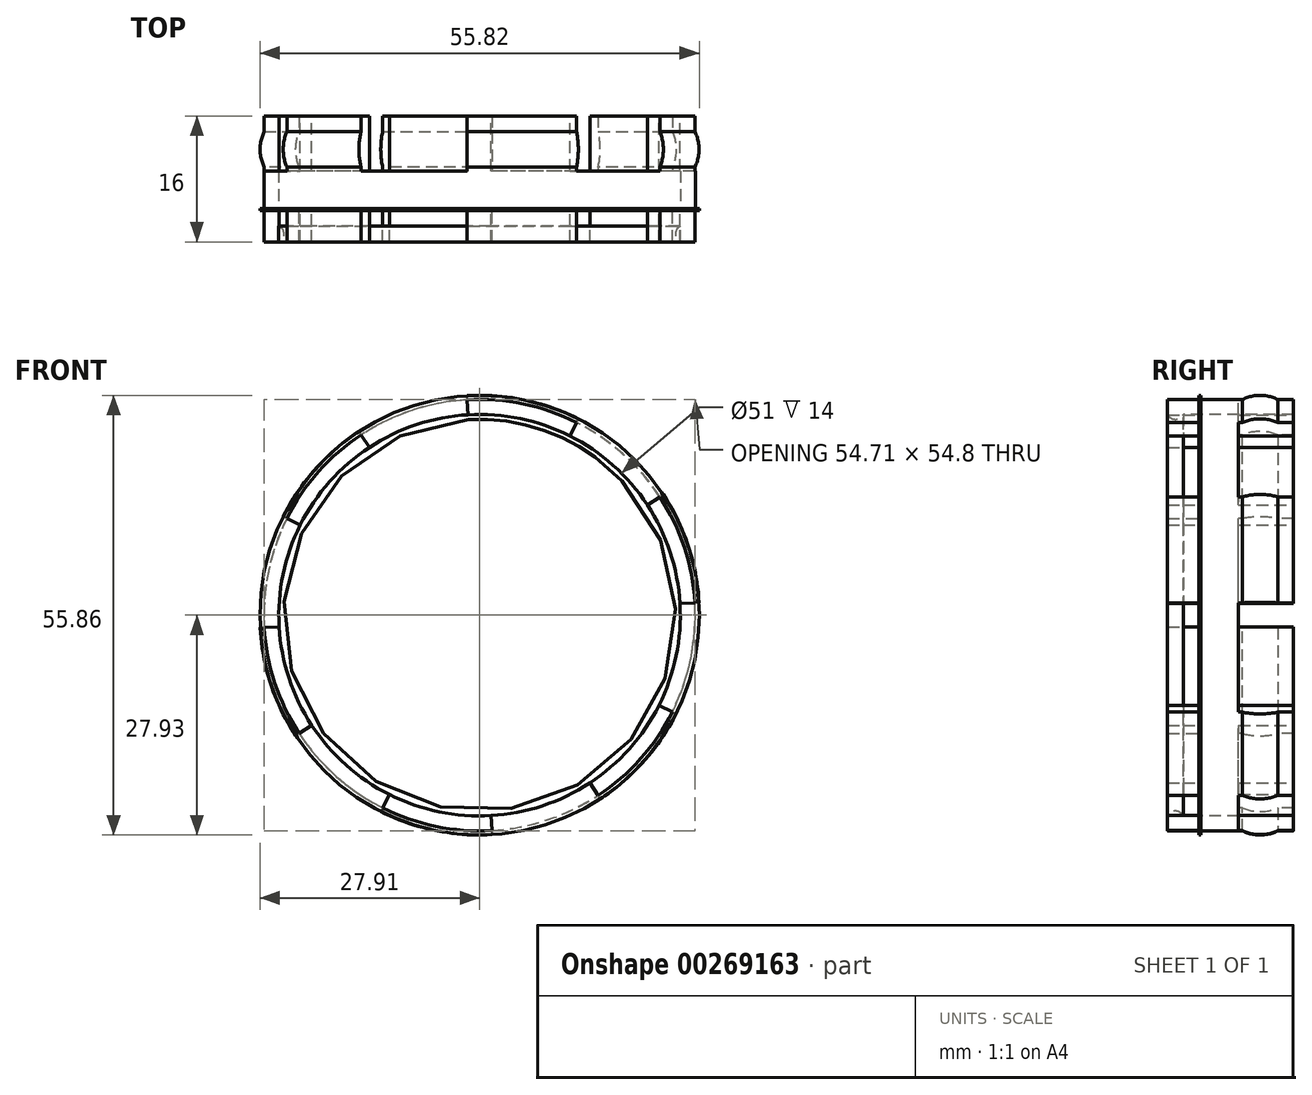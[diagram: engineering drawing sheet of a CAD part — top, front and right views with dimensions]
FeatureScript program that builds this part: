
annotation { "Feature Type Name" : "Feature", "Feature Type Description" : "" }
export const myFeature = defineFeature(function(context is Context, id is Id, definition is map)
    precondition{}
    {
        {
            var Q0;
            Q0=qCreatedBy(makeId("Front.planeOp"),FACE);
            var sketch = newSketch(context, id + "F0", { "sketchPlane" : qUnion([Q0])});
            skCircle(sketch, "E0", {"center": v(0, 0) * mm, "radius": 32.7 * mm});
            skCircle(sketch, "E1", {"center": v(0, 0) * mm, "radius": 27.2 * mm});
            skCircle(sketch, "E2", {"center": v(0, 0) * mm, "radius": 25.8 * mm});
            skSolve(sketch);
        }
        {
            var Q0;
            Q0=makeQuery(id+"F0.imprint","IMPRINT",FACE,{"disambiguationData":[TD([[makeQuery(id+"F0.imprint","IMPRINT",EDGE,{"derivedFrom":sQuery(id+"F0.wireOp",EDGE,"E0")}),1.0]])]});
            var Q1;
            Q1=makeQuery(id+"F0.imprint","IMPRINT",FACE,{"disambiguationData":[TD([[makeQuery(id+"F0.imprint","IMPRINT",EDGE,{"derivedFrom":sQuery(id+"F0.wireOp",EDGE,"E2")}),1.0]])]});
            var Q2;
            Q2=makeQuery(id+"F0.imprint","IMPRINT",FACE,{"disambiguationData":[TD([[makeQuery(id+"F0.imprint","IMPRINT",EDGE,{"derivedFrom":sQuery(id+"F0.wireOp",EDGE,"E1")}),1.0]])]});
            extrude(context, id + "F1", {"entities" : qUnion([Q0, Q1, Q2]), "depth" : 2 * mm});
        }
        {
            var Q0;
            Q0=makeQuery(id+"F1.opExtrude","CAP_FACE",FACE,{"disambiguationData":[OSD([sQuery(id+"F0.wireOp",EDGE,"E0")])],"isStart":true});
            var sketch = newSketch(context, id + "F2", { "sketchPlane" : qUnion([Q0])});
            skCircle(sketch, "E3", {"center": v(0, 0) * mm, "radius": 27.4 * mm});
            skCircle(sketch, "E4", {"center": v(0, 0) * mm, "radius": 25.5 * mm});
            skSolve(sketch);
        }
        {
            var Q0;
            Q0 = qSketchRegion(id + "F2", true);
            extrude(context, id + "F3", {"entities" : qUnion([Q0]), "operationType" : NewBodyOperationType.ADD, "depth" : 12 * mm});
        }
        {
            var Q0;
            {var subQ0=sQuery(id+"F0.wireOp",EDGE,"E0");Q0=makeQuery(id+"F3.boolean.opBoolean","SPLIT",FACE,{"disambiguationData":[TD([makeQuery(id+"F1.opExtrude","SWEPT_FACE",FACE,{"disambiguationData":[OSD([subQ0])]})])],"derivedFrom":makeQuery(id+"F1.opExtrude","CAP_FACE",FACE,{"disambiguationData":[OSD([subQ0])],"isStart":true})});}
            cPlane(context, id + "F4", {"entities" : qUnion([Q0]), "cplaneType" : CPlaneType.OFFSET, "offset" : 7.75 * mm, "width" : 152.4 * mm, "height" : 152.4 * mm});
        }
        {
            var Q0;
            Q0=qCreatedBy(makeId("Top.planeOp"),FACE);
            var sketch = newSketch(context, id + "F5", { "sketchPlane" : qUnion([Q0])});
            skLineSegment(sketch, "E5", {"start": v(27.4, 12) * mm, "end": v(27.4, 0) * mm});
            skArc(sketch, "E6", {"start": v(27.4, 5.5) * mm, "mid": v(27.93, 7.75) * mm, "end": v(27.4, 10) * mm});
            skSolve(sketch);
        }
        {
            var Q0;
            Q0=qCreatedBy(makeId("Right.planeOp"),FACE);
            var sketch = newSketch(context, id + "F6", { "sketchPlane" : qUnion([Q0])});
            skLineSegment(sketch, "E7", {"start": v(44.22, 0) * mm, "end": v(-14.52, 0) * mm});
            skSolve(sketch);
        }
        {
            var Q0;
            Q0 = qSketchRegion(id + "F5", true);
            var Q1;
            Q1=sQuery(id+"F6.wireOp",EDGE,"E7");
            revolve(context, id + "F7", {"operationType" : NewBodyOperationType.ADD, "entities" : qUnion([Q0]), "axis" : qUnion([Q1]), "revolveType" : RevolveType.FULL});
        }
        {
            var Q0;
            Q0=makeQuery(id+"F3.opExtrude","CAP_FACE",FACE,{"disambiguationData":[OSD([sQuery(id+"F2.wireOp",EDGE,"E3"),sQuery(id+"F2.wireOp",EDGE,"E4")])],"isStart":false});
            var sketch = newSketch(context, id + "F8", { "sketchPlane" : qUnion([Q0])});
            skArc(sketch, "E8.cCircle", {"start": v(-23.64, -11.9) * mm, "mid": v(-19.76, -17.6) * mm, "end": v(-14.53, -22.12) * mm, "construction": true});
            skLineSegment(sketch, "E8.1", {"start": v(15.04, 22.9) * mm, "end": v(24.48, 12.31) * mm});
            skLineSegment(sketch, "E8.3", {"start": v(27.35, -1.58) * mm, "end": v(22.9, -15.04) * mm});
            skLineSegment(sketch, "E8.5", {"start": v(12.31, -24.48) * mm, "end": v(-1.58, -27.35) * mm});
            skLineSegment(sketch, "E8.7", {"start": v(-15.04, -22.9) * mm, "end": v(-24.48, -12.31) * mm});
            skLineSegment(sketch, "E8.9", {"start": v(-27.35, 1.58) * mm, "end": v(-22.9, 15.04) * mm});
            skLineSegment(sketch, "E8.11", {"start": v(-12.31, 24.48) * mm, "end": v(1.58, 27.35) * mm});
            skPoint(sketch, "E8.0.midPoint", {"position": v(8.3, 25.13) * mm});
            skLineSegment(sketch, "E9", {"start": v(-27.35, 1.58) * mm, "end": v(0, 0) * mm});
            skLineSegment(sketch, "E10", {"start": v(-24.48, -12.31) * mm, "end": v(0, 0) * mm});
            skLineSegment(sketch, "E11", {"start": v(-24.48, -12.31) * mm, "end": v(-32.97, -16.58) * mm});
            skLineSegment(sketch, "E12", {"start": v(-27.35, 1.58) * mm, "end": v(-35.6, 2.05) * mm});
            skLineSegment(sketch, "E13", {"start": v(-35.6, 2.05) * mm, "end": v(-32.97, -16.58) * mm});
            skLineSegment(sketch, "E14", {"start": v(0, 0) * mm, "end": v(-15.04, -22.9) * mm});
            skLineSegment(sketch, "E15", {"start": v(-1.58, -27.35) * mm, "end": v(0, 0) * mm});
            skLineSegment(sketch, "E16", {"start": v(-15.04, -22.9) * mm, "end": v(-20.27, -30.87) * mm});
            skLineSegment(sketch, "E17", {"start": v(-1.58, -27.35) * mm, "end": v(-2.08, -36.1) * mm});
            skLineSegment(sketch, "E18", {"start": v(-2.08, -36.1) * mm, "end": v(-20.27, -30.87) * mm});
            skArc(sketch, "E19.trimOffspring", {"start": v(-1.52, -26.42) * mm, "mid": v(5.37, -25.92) * mm, "end": v(11.9, -23.64) * mm, "construction": true});
            skLineSegment(sketch, "E20", {"start": v(0, 0) * mm, "end": v(12.31, -24.48) * mm});
            skLineSegment(sketch, "E21", {"start": v(0, 0) * mm, "end": v(22.9, -15.04) * mm});
            skLineSegment(sketch, "E22", {"start": v(12.31, -24.48) * mm, "end": v(16.41, -32.63) * mm});
            skLineSegment(sketch, "E23", {"start": v(22.9, -15.04) * mm, "end": v(29.2, -19.18) * mm});
            skLineSegment(sketch, "E24", {"start": v(29.2, -19.18) * mm, "end": v(16.41, -32.63) * mm});
            skArc(sketch, "E25.trimOffspring", {"start": v(22.12, -14.53) * mm, "mid": v(25.13, -8.3) * mm, "end": v(26.42, -1.52) * mm, "construction": true});
            skLineSegment(sketch, "E26", {"start": v(0, 0) * mm, "end": v(24.48, 12.31) * mm});
            skLineSegment(sketch, "E27", {"start": v(27.35, -1.58) * mm, "end": v(0, 0) * mm});
            skLineSegment(sketch, "E28", {"start": v(27.35, -1.58) * mm, "end": v(35.67, -2.05) * mm});
            skLineSegment(sketch, "E29", {"start": v(24.48, 12.31) * mm, "end": v(31.5, 15.85) * mm});
            skLineSegment(sketch, "E30", {"start": v(31.5, 15.85) * mm, "end": v(35.67, -2.05) * mm});
            skArc(sketch, "E31.trimOffspring", {"start": v(23.64, 11.9) * mm, "mid": v(19.76, 17.6) * mm, "end": v(14.53, 22.12) * mm, "construction": true});
            skLineSegment(sketch, "E32", {"start": v(15.04, 22.9) * mm, "end": v(0, 0) * mm});
            skLineSegment(sketch, "E33", {"start": v(0, 0.13) * mm, "end": v(1.58, 27.35) * mm});
            skLineSegment(sketch, "E34", {"start": v(1.58, 27.35) * mm, "end": v(2.08, 36.13) * mm});
            skLineSegment(sketch, "E35", {"start": v(15.04, 22.9) * mm, "end": v(20.6, 31.37) * mm});
            skLineSegment(sketch, "E36", {"start": v(20.6, 31.37) * mm, "end": v(2.08, 36.13) * mm});
            skArc(sketch, "E37.trimOffspring", {"start": v(1.52, 26.42) * mm, "mid": v(-5.37, 25.92) * mm, "end": v(-11.9, 23.64) * mm, "construction": true});
            skLineSegment(sketch, "E38", {"start": v(0, 0) * mm, "end": v(-22.9, 15.04) * mm});
            skLineSegment(sketch, "E39", {"start": v(0, 0) * mm, "end": v(-12.31, 24.48) * mm});
            skLineSegment(sketch, "E40", {"start": v(-12.31, 24.48) * mm, "end": v(-16.96, 33.71) * mm});
            skLineSegment(sketch, "E41", {"start": v(-22.9, 15.04) * mm, "end": v(-31.87, 20.93) * mm});
            skLineSegment(sketch, "E42", {"start": v(-31.87, 20.93) * mm, "end": v(-16.96, 33.71) * mm});
            skArc(sketch, "E43.trimOffspring", {"start": v(-22.12, 14.53) * mm, "mid": v(-25.13, 8.3) * mm, "end": v(-26.42, 1.52) * mm, "construction": true});
            skCircle(sketch, "E44.0", {"center": v(0, 0) * mm, "radius": 32.7 * mm});
            skSolve(sketch);
        }
        {
            var Q0;
            {var subQ0=sQuery(id+"F8.wireOp",EDGE,"E9");var subQ3=makeQuery(id+"F3.opExtrude","CAP_EDGE",EDGE,{"disambiguationData":[OSD([sQuery(id+"F2.wireOp",EDGE,"E4")])],"isStart":false});var subQ4=makeQuery(id+"F8.imprint","INTERSECT",VERTEX,{"derivedFrom":[subQ3,subQ0]});Q0=makeQuery(id+"F8.imprint","IMPRINT",FACE,{"disambiguationData":[TD([[makeQuery(id+"F8.imprint","IMPRINT",EDGE,{"disambiguationData":[TD([[subQ4,-1.0]])],"derivedFrom":subQ3}),-1.0]])]});}
            var Q1;
            {var subQ0=sQuery(id+"F8.wireOp",EDGE,"E11");Q1=makeQuery(id+"F8.imprint","IMPRINT",FACE,{"disambiguationData":[TD([[makeQuery(id+"F8.imprint","IMPRINT",EDGE,{"derivedFrom":subQ0}),-1.0]])]});}
            var Q2;
            {var subQ0=sQuery(id+"F8.wireOp",EDGE,"E14");var subQ3=makeQuery(id+"F3.opExtrude","CAP_EDGE",EDGE,{"disambiguationData":[OSD([sQuery(id+"F2.wireOp",EDGE,"E4")])],"isStart":false});var subQ4=makeQuery(id+"F8.imprint","INTERSECT",VERTEX,{"derivedFrom":[subQ3,subQ0]});Q2=makeQuery(id+"F8.imprint","IMPRINT",FACE,{"disambiguationData":[TD([[makeQuery(id+"F8.imprint","IMPRINT",EDGE,{"disambiguationData":[TD([[subQ4,-1.0]])],"derivedFrom":subQ3}),-1.0]])]});}
            var Q3;
            {var subQ0=sQuery(id+"F8.wireOp",EDGE,"E16");Q3=makeQuery(id+"F8.imprint","IMPRINT",FACE,{"disambiguationData":[TD([[makeQuery(id+"F8.imprint","IMPRINT",EDGE,{"derivedFrom":subQ0}),1.0]])]});}
            var Q4;
            {var subQ0=sQuery(id+"F8.wireOp",EDGE,"E20");var subQ3=makeQuery(id+"F3.opExtrude","CAP_EDGE",EDGE,{"disambiguationData":[OSD([sQuery(id+"F2.wireOp",EDGE,"E4")])],"isStart":false});var subQ4=makeQuery(id+"F8.imprint","INTERSECT",VERTEX,{"derivedFrom":[subQ3,subQ0]});Q4=makeQuery(id+"F8.imprint","IMPRINT",FACE,{"disambiguationData":[TD([[makeQuery(id+"F8.imprint","IMPRINT",EDGE,{"disambiguationData":[TD([[subQ4,-1.0]])],"derivedFrom":subQ3}),-1.0]])]});}
            var Q5;
            {var subQ0=sQuery(id+"F8.wireOp",EDGE,"E22");Q5=makeQuery(id+"F8.imprint","IMPRINT",FACE,{"disambiguationData":[TD([[makeQuery(id+"F8.imprint","IMPRINT",EDGE,{"derivedFrom":subQ0}),1.0]])]});}
            var Q6;
            {var subQ0=sQuery(id+"F8.wireOp",EDGE,"E26");var subQ3=makeQuery(id+"F3.opExtrude","CAP_EDGE",EDGE,{"disambiguationData":[OSD([sQuery(id+"F2.wireOp",EDGE,"E4")])],"isStart":false});var subQ4=makeQuery(id+"F8.imprint","INTERSECT",VERTEX,{"derivedFrom":[subQ3,subQ0]});Q6=makeQuery(id+"F8.imprint","IMPRINT",FACE,{"disambiguationData":[TD([[makeQuery(id+"F8.imprint","IMPRINT",EDGE,{"disambiguationData":[TD([[subQ4,1.0]])],"derivedFrom":subQ3}),-1.0]])]});}
            var Q7;
            {var subQ0=sQuery(id+"F8.wireOp",EDGE,"E28");Q7=makeQuery(id+"F8.imprint","IMPRINT",FACE,{"disambiguationData":[TD([[makeQuery(id+"F8.imprint","IMPRINT",EDGE,{"derivedFrom":subQ0}),1.0]])]});}
            var Q8;
            {var subQ3=makeQuery(id+"F3.opExtrude","CAP_EDGE",EDGE,{"disambiguationData":[OSD([sQuery(id+"F2.wireOp",EDGE,"E4")])],"isStart":false});var subQ5=sQuery(id+"F8.wireOp",EDGE,"E33");var subQ7=makeQuery(id+"F8.imprint","INTERSECT",VERTEX,{"derivedFrom":[subQ3,subQ5]});Q8=makeQuery(id+"F8.imprint","IMPRINT",FACE,{"disambiguationData":[TD([[makeQuery(id+"F8.imprint","IMPRINT",EDGE,{"disambiguationData":[TD([[subQ7,1.0]])],"derivedFrom":subQ3}),-1.0]])]});}
            var Q9;
            {var subQ0=sQuery(id+"F8.wireOp",EDGE,"E34");Q9=makeQuery(id+"F8.imprint","IMPRINT",FACE,{"disambiguationData":[TD([[makeQuery(id+"F8.imprint","IMPRINT",EDGE,{"derivedFrom":subQ0}),-1.0]])]});}
            var Q10;
            {var subQ0=sQuery(id+"F8.wireOp",EDGE,"E38");var subQ3=makeQuery(id+"F3.opExtrude","CAP_EDGE",EDGE,{"disambiguationData":[OSD([sQuery(id+"F2.wireOp",EDGE,"E4")])],"isStart":false});var subQ4=makeQuery(id+"F8.imprint","INTERSECT",VERTEX,{"derivedFrom":[subQ3,subQ0]});Q10=makeQuery(id+"F8.imprint","IMPRINT",FACE,{"disambiguationData":[TD([[makeQuery(id+"F8.imprint","IMPRINT",EDGE,{"disambiguationData":[TD([[subQ4,1.0]])],"derivedFrom":subQ3}),-1.0]])]});}
            var Q11;
            {var subQ0=sQuery(id+"F8.wireOp",EDGE,"E40");Q11=makeQuery(id+"F8.imprint","IMPRINT",FACE,{"disambiguationData":[TD([[makeQuery(id+"F8.imprint","IMPRINT",EDGE,{"derivedFrom":subQ0}),1.0]])]});}
            extrude(context, id + "F9", {"entities" : qUnion([Q0, Q1, Q2, Q3, Q4, Q5, Q6, Q7, Q8, Q9, Q10, Q11]), "operationType" : NewBodyOperationType.REMOVE, "oppositeDirection" : true, "depth" : 7 * mm});
        }
        {
            var Q0;
            Q0=makeQuery(id+"F3.boolean.opBoolean","SPLIT",FACE,{"disambiguationData":[TD([makeQuery(id+"F3.opExtrude","SWEPT_FACE",FACE,{"disambiguationData":[OSD([sQuery(id+"F2.wireOp",EDGE,"E4")])]})])],"derivedFrom":makeQuery(id+"F1.opExtrude","CAP_FACE",FACE,{"disambiguationData":[OSD([sQuery(id+"F0.wireOp",EDGE,"E0")])],"isStart":true})});
            var sketch = newSketch(context, id + "F10", { "sketchPlane" : qUnion([Q0])});
            skCircle(sketch, "E45", {"center": v(0, 0) * mm, "radius": 34.62 * mm});
            skSolve(sketch);
        }
        {
            var Q0;
            Q0 = qSketchRegion(id + "F10", true);
            extrude(context, id + "F11", {"entities" : qUnion([Q0]), "operationType" : NewBodyOperationType.REMOVE, "oppositeDirection" : true, "depth" : 25.4 * mm});
        }
        {
            var Q0;
            {var subQ0=sQuery(id+"F2.wireOp",EDGE,"E3");var subQ1=sQuery(id+"F2.wireOp",EDGE,"E4");Q0=makeQuery(id+"F9.boolean.opBoolean","SPLIT",FACE,{"disambiguationData":[TD([makeQuery(id+"F9.opExtrude","SWEPT_FACE",FACE,{"disambiguationData":[OSD([sQuery(id+"F8.wireOp",EDGE,"E21"),sQuery(id+"F8.wireOp",EDGE,"E23")])]})])],"derivedFrom":makeQuery(id+"F3.opExtrude","CAP_FACE",FACE,{"disambiguationData":[OSD([subQ0,subQ1])],"isStart":false})});}
            var Q1;
            {var subQ0=sQuery(id+"F2.wireOp",EDGE,"E3");var subQ1=sQuery(id+"F2.wireOp",EDGE,"E4");Q1=makeQuery(id+"F9.boolean.opBoolean","SPLIT",FACE,{"disambiguationData":[TD([makeQuery(id+"F9.opExtrude","SWEPT_FACE",FACE,{"disambiguationData":[OSD([sQuery(id+"F8.wireOp",EDGE,"E15"),sQuery(id+"F8.wireOp",EDGE,"E17")])]})])],"derivedFrom":makeQuery(id+"F3.opExtrude","CAP_FACE",FACE,{"disambiguationData":[OSD([subQ0,subQ1])],"isStart":false})});}
            var Q2;
            {var subQ0=sQuery(id+"F2.wireOp",EDGE,"E3");var subQ1=sQuery(id+"F2.wireOp",EDGE,"E4");Q2=makeQuery(id+"F9.boolean.opBoolean","SPLIT",FACE,{"disambiguationData":[TD([makeQuery(id+"F9.opExtrude","SWEPT_FACE",FACE,{"disambiguationData":[OSD([sQuery(id+"F8.wireOp",EDGE,"E10"),sQuery(id+"F8.wireOp",EDGE,"E11")])]})])],"derivedFrom":makeQuery(id+"F3.opExtrude","CAP_FACE",FACE,{"disambiguationData":[OSD([subQ0,subQ1])],"isStart":false})});}
            var Q3;
            {var subQ0=sQuery(id+"F2.wireOp",EDGE,"E3");var subQ1=sQuery(id+"F2.wireOp",EDGE,"E4");Q3=makeQuery(id+"F9.boolean.opBoolean","SPLIT",FACE,{"disambiguationData":[TD([makeQuery(id+"F9.opExtrude","SWEPT_FACE",FACE,{"disambiguationData":[OSD([sQuery(id+"F8.wireOp",EDGE,"E9"),sQuery(id+"F8.wireOp",EDGE,"E12")])]})])],"derivedFrom":makeQuery(id+"F3.opExtrude","CAP_FACE",FACE,{"disambiguationData":[OSD([subQ0,subQ1])],"isStart":false})});}
            var Q4;
            {var subQ0=sQuery(id+"F2.wireOp",EDGE,"E3");var subQ1=sQuery(id+"F2.wireOp",EDGE,"E4");Q4=makeQuery(id+"F9.boolean.opBoolean","SPLIT",FACE,{"disambiguationData":[TD([makeQuery(id+"F9.opExtrude","SWEPT_FACE",FACE,{"disambiguationData":[OSD([sQuery(id+"F8.wireOp",EDGE,"E33"),sQuery(id+"F8.wireOp",EDGE,"E34")])]})])],"derivedFrom":makeQuery(id+"F3.opExtrude","CAP_FACE",FACE,{"disambiguationData":[OSD([subQ0,subQ1])],"isStart":false})});}
            var Q5;
            {var subQ0=sQuery(id+"F2.wireOp",EDGE,"E3");var subQ1=sQuery(id+"F2.wireOp",EDGE,"E4");Q5=makeQuery(id+"F9.boolean.opBoolean","SPLIT",FACE,{"disambiguationData":[TD([makeQuery(id+"F9.opExtrude","SWEPT_FACE",FACE,{"disambiguationData":[OSD([sQuery(id+"F8.wireOp",EDGE,"E26"),sQuery(id+"F8.wireOp",EDGE,"E29")])]})])],"derivedFrom":makeQuery(id+"F3.opExtrude","CAP_FACE",FACE,{"disambiguationData":[OSD([subQ0,subQ1])],"isStart":false})});}
            extrude(context, id + "F12", {"entities" : qUnion([Q0, Q1, Q2, Q3, Q4, Q5]), "operationType" : NewBodyOperationType.ADD, "oppositeDirection" : true, "depth" : 16 * mm});
        }
        {
            var Q0;
            Q0=makeQuery(id+"F12.opExtrude","SWEPT_FACE",FACE,{"disambiguationData":[OSD([sQuery(id+"F8.wireOp",EDGE,"E15"),sQuery(id+"F8.wireOp",EDGE,"E17")])]});
            var sketch = newSketch(context, id + "F13", { "sketchPlane" : qUnion([Q0])});
            skArc(sketch, "E46", {"start": v(-2, -25.5) * mm, "mid": v(-3, -24.88) * mm, "end": v(-4, -25.5) * mm});
            skSolve(sketch);
        }
        {
            var Q0;
            {var subQ0=sQuery(id+"F13.wireOp",EDGE,"E46");Q0=makeQuery(id+"F13.imprint","IMPRINT",FACE,{"disambiguationData":[TD([[makeQuery(id+"F13.imprint","IMPRINT",EDGE,{"derivedFrom":subQ0}),1.0]])]});}
            var Q1;
            Q1=sQuery(id+"F6.wireOp",EDGE,"E7");
            revolve(context, id + "F14", {"operationType" : NewBodyOperationType.ADD, "entities" : qUnion([Q0]), "axis" : qUnion([Q1]), "revolveType" : RevolveType.FULL});
        }
        {
            var Q0;
            {var subQ9=sQuery(id+"F8.wireOp",EDGE,"E12");var subQ10=sQuery(id+"F8.wireOp",EDGE,"E9");Q0=makeQuery(id+"F12.boolean.opBoolean","SPLIT",FACE,{"disambiguationData":[TD([makeQuery(id+"F12.opExtrude","SWEPT_FACE",FACE,{"disambiguationData":[OSD([subQ10,subQ9])]})])],"derivedFrom":makeQuery(id+"F11.boolean.opBoolean","COPY",FACE,{"derivedFrom":makeQuery(id+"F11.opExtrude","CAP_FACE",FACE,{"disambiguationData":[OSD([sQuery(id+"F10.wireOp",EDGE,"E45")])],"isStart":true})})});}
            var sketch = newSketch(context, id + "F15", { "sketchPlane" : qUnion([Q0])});
            skLineSegment(sketch, "E47", {"start": v(24.48, -12.31) * mm, "end": v(0, 0) * mm});
            skLineSegment(sketch, "E48", {"start": v(0, 0) * mm, "end": v(27.35, 1.58) * mm});
            skLineSegment(sketch, "E49.0.0", {"start": v(12.31, 24.48) * mm, "end": v(11.46, 22.78) * mm});
            skArc(sketch, "E49.0.1", {"start": v(11.46, 22.78) * mm, "mid": v(16.96, 19.04) * mm, "end": v(21.31, 14) * mm});
            skLineSegment(sketch, "E49.0.2", {"start": v(21.31, 14) * mm, "end": v(22.9, 15.04) * mm});
            skArc(sketch, "E49.0.3", {"start": v(22.9, 15.04) * mm, "mid": v(18.23, 20.46) * mm, "end": v(12.31, 24.48) * mm});
            skArc(sketch, "E50.0.0", {"start": v(-14, 21.31) * mm, "mid": v(-8, 24.21) * mm, "end": v(-1.47, 25.46) * mm});
            skLineSegment(sketch, "E50.0.1", {"start": v(-1.47, 25.46) * mm, "end": v(-1.58, 27.35) * mm});
            skArc(sketch, "E50.0.2", {"start": v(-1.58, 27.35) * mm, "mid": v(-8.6, 26.01) * mm, "end": v(-15.04, 22.9) * mm});
            skLineSegment(sketch, "E50.0.3", {"start": v(-15.04, 22.9) * mm, "end": v(-14, 21.31) * mm});
            skArc(sketch, "E51.0.0", {"start": v(-25.46, -1.47) * mm, "mid": v(-24.97, 5.17) * mm, "end": v(-22.78, 11.46) * mm});
            skLineSegment(sketch, "E51.0.1", {"start": v(-22.78, 11.46) * mm, "end": v(-24.48, 12.31) * mm});
            skArc(sketch, "E51.0.2", {"start": v(-24.48, 12.31) * mm, "mid": v(-26.83, 5.56) * mm, "end": v(-27.35, -1.58) * mm});
            skLineSegment(sketch, "E51.0.3", {"start": v(-27.35, -1.58) * mm, "end": v(-25.46, -1.47) * mm});
            skArc(sketch, "E52.0.0", {"start": v(-11.46, -22.78) * mm, "mid": v(-16.96, -19.04) * mm, "end": v(-21.31, -14) * mm});
            skLineSegment(sketch, "E52.0.1", {"start": v(-21.31, -14) * mm, "end": v(-22.9, -15.04) * mm});
            skArc(sketch, "E52.0.2", {"start": v(-22.9, -15.04) * mm, "mid": v(-18.23, -20.46) * mm, "end": v(-12.31, -24.48) * mm});
            skLineSegment(sketch, "E52.0.3", {"start": v(-12.31, -24.48) * mm, "end": v(-11.46, -22.78) * mm});
            skLineSegment(sketch, "E53.0.0", {"start": v(1.47, -25.46) * mm, "end": v(1.58, -27.35) * mm});
            skArc(sketch, "E53.0.1", {"start": v(1.58, -27.35) * mm, "mid": v(8.6, -26.01) * mm, "end": v(15.04, -22.9) * mm});
            skLineSegment(sketch, "E53.0.2", {"start": v(15.04, -22.9) * mm, "end": v(14, -21.31) * mm});
            skArc(sketch, "E53.0.3", {"start": v(14, -21.31) * mm, "mid": v(8, -24.21) * mm, "end": v(1.47, -25.46) * mm});
            skLineSegment(sketch, "E54", {"start": v(0, 0) * mm, "end": v(15.04, -22.9) * mm});
            skLineSegment(sketch, "E55", {"start": v(0, 0) * mm, "end": v(1.58, -27.35) * mm});
            skLineSegment(sketch, "E56", {"start": v(-12.31, -24.48) * mm, "end": v(0, 0) * mm});
            skLineSegment(sketch, "E57", {"start": v(-22.9, -15.04) * mm, "end": v(0, 0) * mm});
            skLineSegment(sketch, "E58", {"start": v(-27.35, -1.58) * mm, "end": v(0, 0) * mm});
            skLineSegment(sketch, "E59", {"start": v(0, 0) * mm, "end": v(-24.48, 12.31) * mm});
            skLineSegment(sketch, "E60", {"start": v(0, 0) * mm, "end": v(-1.58, 27.35) * mm});
            skLineSegment(sketch, "E61", {"start": v(-15.04, 22.9) * mm, "end": v(0, 0) * mm});
            skLineSegment(sketch, "E62", {"start": v(0, 0) * mm, "end": v(12.31, 24.48) * mm});
            skLineSegment(sketch, "E63", {"start": v(22.9, 15.04) * mm, "end": v(0, 0) * mm});
            skSolve(sketch);
        }
        {
            var Q0;
            {var subQ0=sQuery(id+"F15.wireOp",EDGE,"E61");var subQ1=sQuery(id+"F15.wireOp",EDGE,"E50.0.0");var subQ2=makeQuery(id+"F15.imprint","INTERSECT",VERTEX,{"derivedFrom":[subQ1,subQ0]});Q0=makeQuery(id+"F15.imprint","IMPRINT",FACE,{"disambiguationData":[TD([[makeQuery(id+"F15.imprint","IMPRINT",EDGE,{"disambiguationData":[TD([[subQ2,-1.0]])],"derivedFrom":subQ1}),-1.0]])]});}
            var Q1;
            {var subQ0=sQuery(id+"F15.wireOp",EDGE,"E51.0.0");Q1=makeQuery(id+"F15.imprint","IMPRINT",FACE,{"disambiguationData":[TD([[makeQuery(id+"F15.imprint","IMPRINT",EDGE,{"derivedFrom":subQ0}),-1.0]])]});}
            var Q2;
            {var subQ0=sQuery(id+"F15.wireOp",EDGE,"E52.0.0");Q2=makeQuery(id+"F15.imprint","IMPRINT",FACE,{"disambiguationData":[TD([[makeQuery(id+"F15.imprint","IMPRINT",EDGE,{"derivedFrom":subQ0}),-1.0]])]});}
            var Q3;
            {var subQ0=sQuery(id+"F15.wireOp",EDGE,"E53.0.3");Q3=makeQuery(id+"F15.imprint","IMPRINT",FACE,{"disambiguationData":[TD([[makeQuery(id+"F15.imprint","IMPRINT",EDGE,{"derivedFrom":subQ0}),-1.0]])]});}
            var Q4;
            {var subQ1=sQuery(id+"F8.wireOp",EDGE,"E12");var subQ2=sQuery(id+"F8.wireOp",EDGE,"E9");var subQ5=sQuery(id+"F2.wireOp",EDGE,"E4");var subQ9=makeQuery(id+"F12.boolean.opBoolean","SPLIT",EDGE,{"disambiguationData":[TD([makeQuery(id+"F12.opExtrude","SWEPT_FACE",FACE,{"disambiguationData":[OSD([subQ2,subQ1])]})])],"derivedFrom":makeQuery(id+"F3.opExtrude","CAP_EDGE",EDGE,{"disambiguationData":[OSD([subQ5])],"isStart":true})});Q4=makeQuery(id+"F15.imprint","IMPRINT",FACE,{"disambiguationData":[TD([[makeQuery(id+"F15.imprint","IMPRINT",EDGE,{"derivedFrom":subQ9}),-1.0]])]});}
            var Q5;
            {var subQ0=sQuery(id+"F15.wireOp",EDGE,"E49.0.1");Q5=makeQuery(id+"F15.imprint","IMPRINT",FACE,{"disambiguationData":[TD([[makeQuery(id+"F15.imprint","IMPRINT",EDGE,{"derivedFrom":subQ0}),-1.0]])]});}
            extrude(context, id + "F16", {"entities" : qUnion([Q0, Q1, Q2, Q3, Q4, Q5]), "operationType" : NewBodyOperationType.REMOVE, "depth" : 25.4 * mm});
        }
        {
            var Q0;
            Q0=makeQuery(id+"F16.boolean.opBoolean","MERGE",FACE,{"derivedFrom":[makeQuery(id+"F12.opExtrude","SWEPT_FACE",FACE,{"disambiguationData":[OSD([sQuery(id+"F8.wireOp",EDGE,"E21"),sQuery(id+"F8.wireOp",EDGE,"E23")])]}),makeQuery(id+"F16.opExtrude","SWEPT_FACE",FACE,{"disambiguationData":[OSD([sQuery(id+"F15.wireOp",EDGE,"E57")])]})]});
            var sketch = newSketch(context, id + "F17", { "sketchPlane" : qUnion([Q0])});
            skLineSegment(sketch, "E64.bottom", {"start": v(-27.4, 0) * mm, "end": v(-27.9, 0) * mm});
            skLineSegment(sketch, "E64.top", {"start": v(-27.4, -0.25) * mm, "end": v(-27.9, -0.25) * mm});
            skLineSegment(sketch, "E64.left", {"start": v(-27.4, 0) * mm, "end": v(-27.4, -0.25) * mm});
            skLineSegment(sketch, "E64.right", {"start": v(-27.9, 0) * mm, "end": v(-27.9, -0.25) * mm});
            skSolve(sketch);
        }
        {
            var Q0;
            Q0 = qSketchRegion(id + "F17", true);
            var Q1;
            Q1=sQuery(id+"F6.wireOp",EDGE,"E7");
            revolve(context, id + "F18", {"operationType" : NewBodyOperationType.ADD, "entities" : qUnion([Q0]), "axis" : qUnion([Q1]), "revolveType" : RevolveType.FULL});
        }
    });
